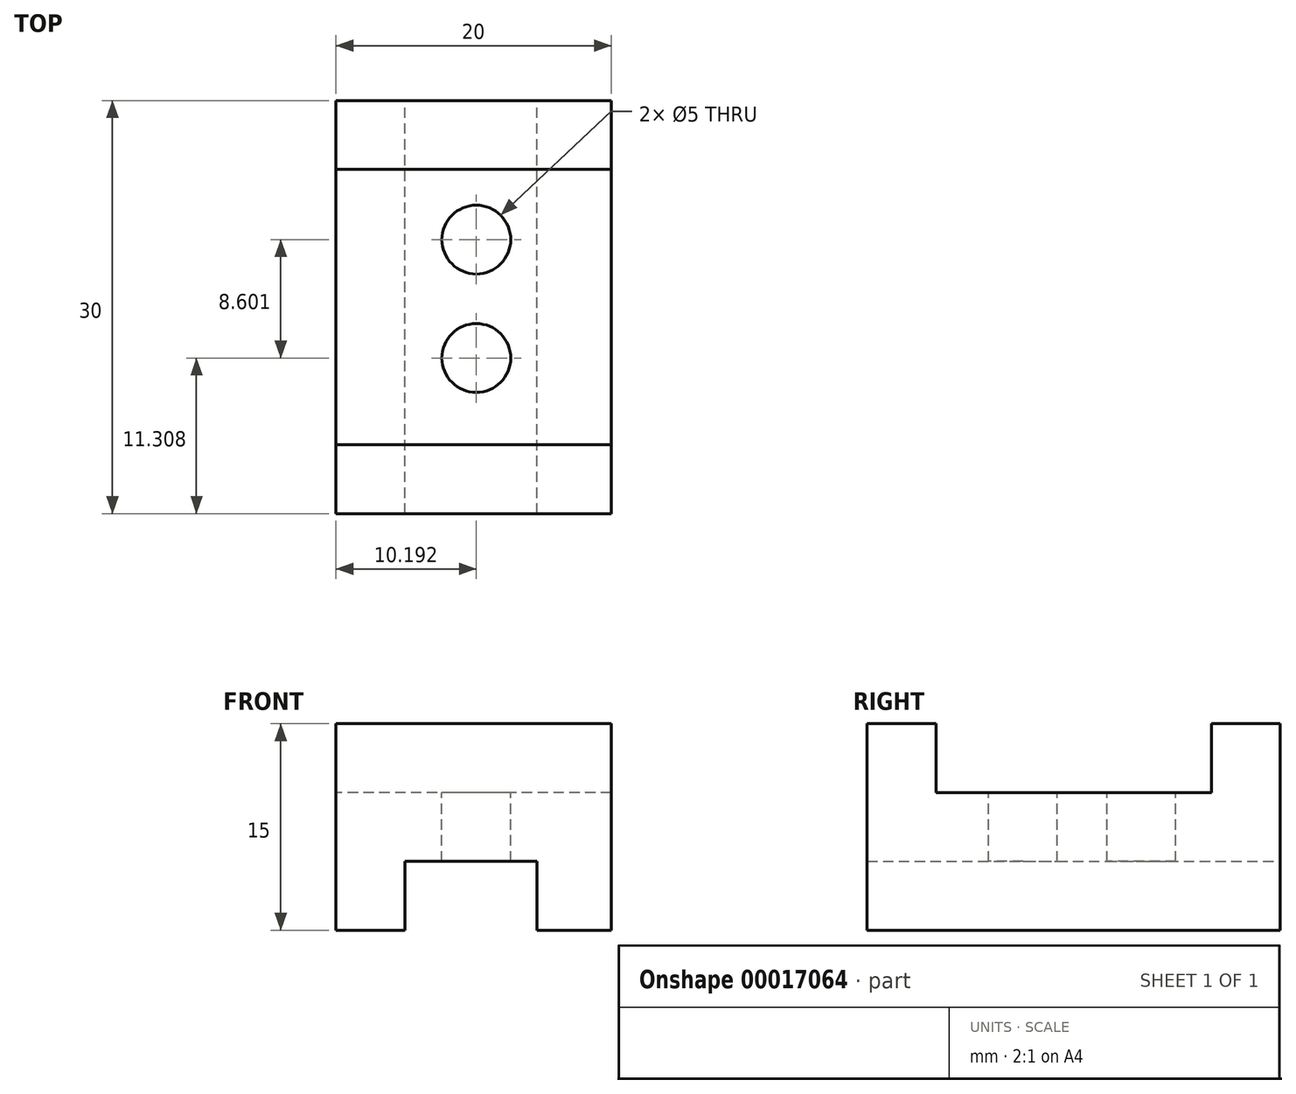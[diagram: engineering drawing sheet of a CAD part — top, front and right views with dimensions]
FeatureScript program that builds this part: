
annotation { "Feature Type Name" : "Feature", "Feature Type Description" : "" }
export const myFeature = defineFeature(function(context is Context, id is Id, definition is map)
    precondition{}
    {
        {
            var Q0;
            Q0=qCreatedBy(makeId("Right.planeOp"),FACE);
            var sketch = newSketch(context, id + "F0", { "sketchPlane" : qUnion([Q0])});
            skLineSegment(sketch, "E0", {"start": v(-16.97, 2.93) * mm, "end": v(-16.97, -12.07) * mm});
            skLineSegment(sketch, "E1", {"start": v(-16.97, -12.07) * mm, "end": v(13.03, -12.07) * mm});
            skLineSegment(sketch, "E2", {"start": v(13.03, -12.07) * mm, "end": v(13.03, 2.93) * mm});
            skLineSegment(sketch, "E3", {"start": v(13.03, 2.93) * mm, "end": v(8.03, 2.93) * mm});
            skLineSegment(sketch, "E4", {"start": v(8.03, 2.93) * mm, "end": v(8.03, -2.07) * mm});
            skLineSegment(sketch, "E5", {"start": v(-16.97, 2.93) * mm, "end": v(-11.97, 2.93) * mm});
            skLineSegment(sketch, "E6", {"start": v(-11.97, 2.93) * mm, "end": v(-11.97, -2.07) * mm});
            skLineSegment(sketch, "E7", {"start": v(-11.97, -2.07) * mm, "end": v(8.03, -2.07) * mm});
            skSolve(sketch);
        }
        {
            var Q0;
            Q0 = qSketchRegion(id + "F0", true);
            extrude(context, id + "F1", {"entities" : qUnion([Q0]), "depth" : 20 * mm});
        }
        {
            var Q0;
            Q0=qCreatedBy(makeId("Front.planeOp"),FACE);
            var sketch = newSketch(context, id + "F2", { "sketchPlane" : qUnion([Q0])});
            skLineSegment(sketch, "E8", {"start": v(5, -12.08) * mm, "end": v(5, -7.08) * mm});
            skLineSegment(sketch, "E9", {"start": v(14.6, -12.07) * mm, "end": v(14.6, -7.08) * mm});
            skLineSegment(sketch, "E10", {"start": v(14.6, -7.08) * mm, "end": v(5, -7.08) * mm});
            skLineSegment(sketch, "E11", {"start": v(5, -12.08) * mm, "end": v(14.6, -12.07) * mm});
            skSolve(sketch);
        }
        {
            var Q0;
            Q0 = qSketchRegion(id + "F2", true);
            extrude(context, id + "F3", {"entities" : qUnion([Q0]), "operationType" : NewBodyOperationType.REMOVE, "endBound" : BoundingType.THROUGH_ALL, "depth" : 25 * mm});
        }
        {
            var Q0;
            Q0=qCreatedBy(makeId("Top.planeOp"),FACE);
            var sketch = newSketch(context, id + "F4", { "sketchPlane" : qUnion([Q0])});
            skCircle(sketch, "E12", {"center": v(10.2, 2.94) * mm, "radius": 2.5 * mm});
            skCircle(sketch, "E13", {"center": v(10.2, -5.66) * mm, "radius": 2.5 * mm});
            skSolve(sketch);
        }
        {
            var Q0;
            Q0 = qSketchRegion(id + "F4", true);
            extrude(context, id + "F5", {"entities" : qUnion([Q0]), "operationType" : NewBodyOperationType.REMOVE, "endBound" : BoundingType.THROUGH_ALL, "oppositeDirection" : true, "depth" : 25 * mm});
        }
        {
            var Q0;
            Q0=makeQuery(id+"F3.boolean.opBoolean","COPY",FACE,{"derivedFrom":makeQuery(id+"F3.opExtrude","CAP_FACE",FACE,{"disambiguationData":[OSD([sQuery(id+"F2.wireOp",EDGE,"E8"),sQuery(id+"F2.wireOp",EDGE,"E9"),sQuery(id+"F2.wireOp",EDGE,"E10"),sQuery(id+"F2.wireOp",EDGE,"E11")])],"isStart":true})});
            extrude(context, id + "F6", {"entities" : qUnion([Q0]), "operationType" : NewBodyOperationType.REMOVE, "endBound" : BoundingType.THROUGH_ALL, "oppositeDirection" : true, "depth" : 25 * mm});
        }
    });
